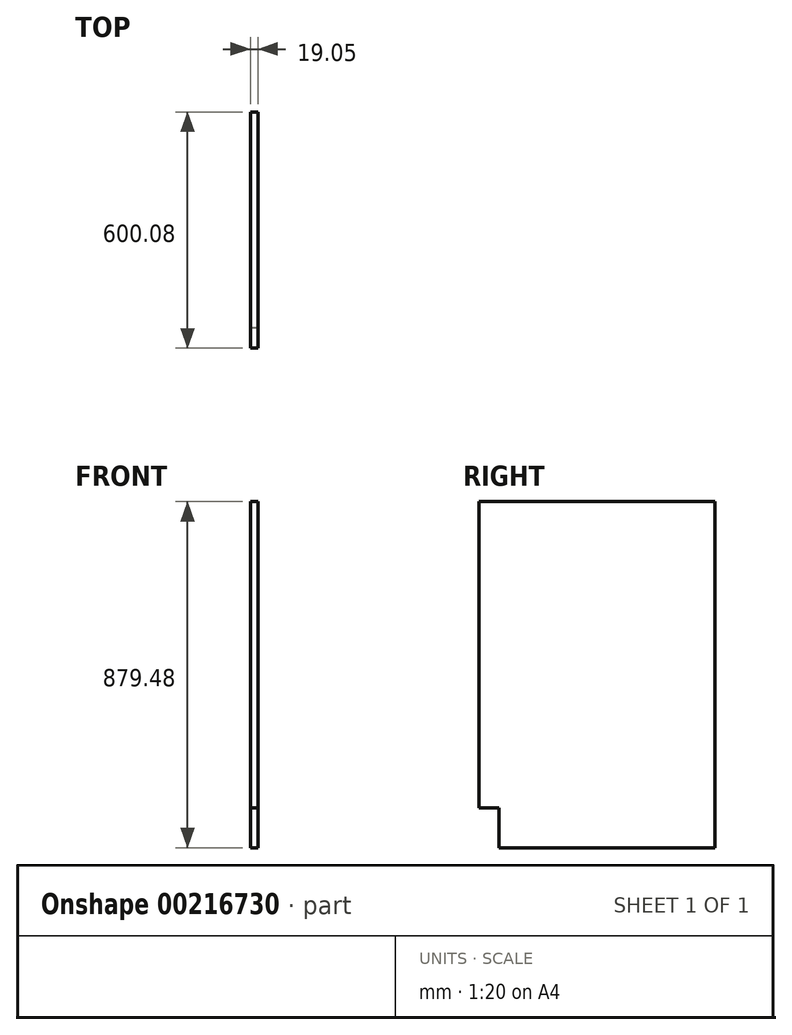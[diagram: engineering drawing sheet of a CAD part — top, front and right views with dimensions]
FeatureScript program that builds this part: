
annotation { "Feature Type Name" : "Feature", "Feature Type Description" : "" }
export const myFeature = defineFeature(function(context is Context, id is Id, definition is map)
    precondition{}
    {
        {
            var Q0;
            Q0=qCreatedBy(makeId("Right.planeOp"),FACE);
            var sketch = newSketch(context, id + "F0", { "sketchPlane" : qUnion([Q0])});
            skLineSegment(sketch, "E0.bottom", {"start": v(50.8, 0) * mm, "end": v(600.08, 0) * mm});
            skLineSegment(sketch, "E0.top", {"start": v(0, 879.48) * mm, "end": v(600.07, 879.48) * mm});
            skLineSegment(sketch, "E0.left", {"start": v(0, 101.6) * mm, "end": v(0, 879.48) * mm});
            skLineSegment(sketch, "E0.right", {"start": v(600.08, 0) * mm, "end": v(600.07, 879.48) * mm});
            skLineSegment(sketch, "E1.top", {"start": v(0, 101.6) * mm, "end": v(50.8, 101.6) * mm});
            skLineSegment(sketch, "E1.right", {"start": v(50.8, 0) * mm, "end": v(50.8, 101.6) * mm});
            skSolve(sketch);
        }
        {
            var Q0;
            Q0 = qSketchRegion(id + "F0", true);
            extrude(context, id + "F1", {"entities" : qUnion([Q0]), "depth" : 19.05 * mm});
        }
    });
